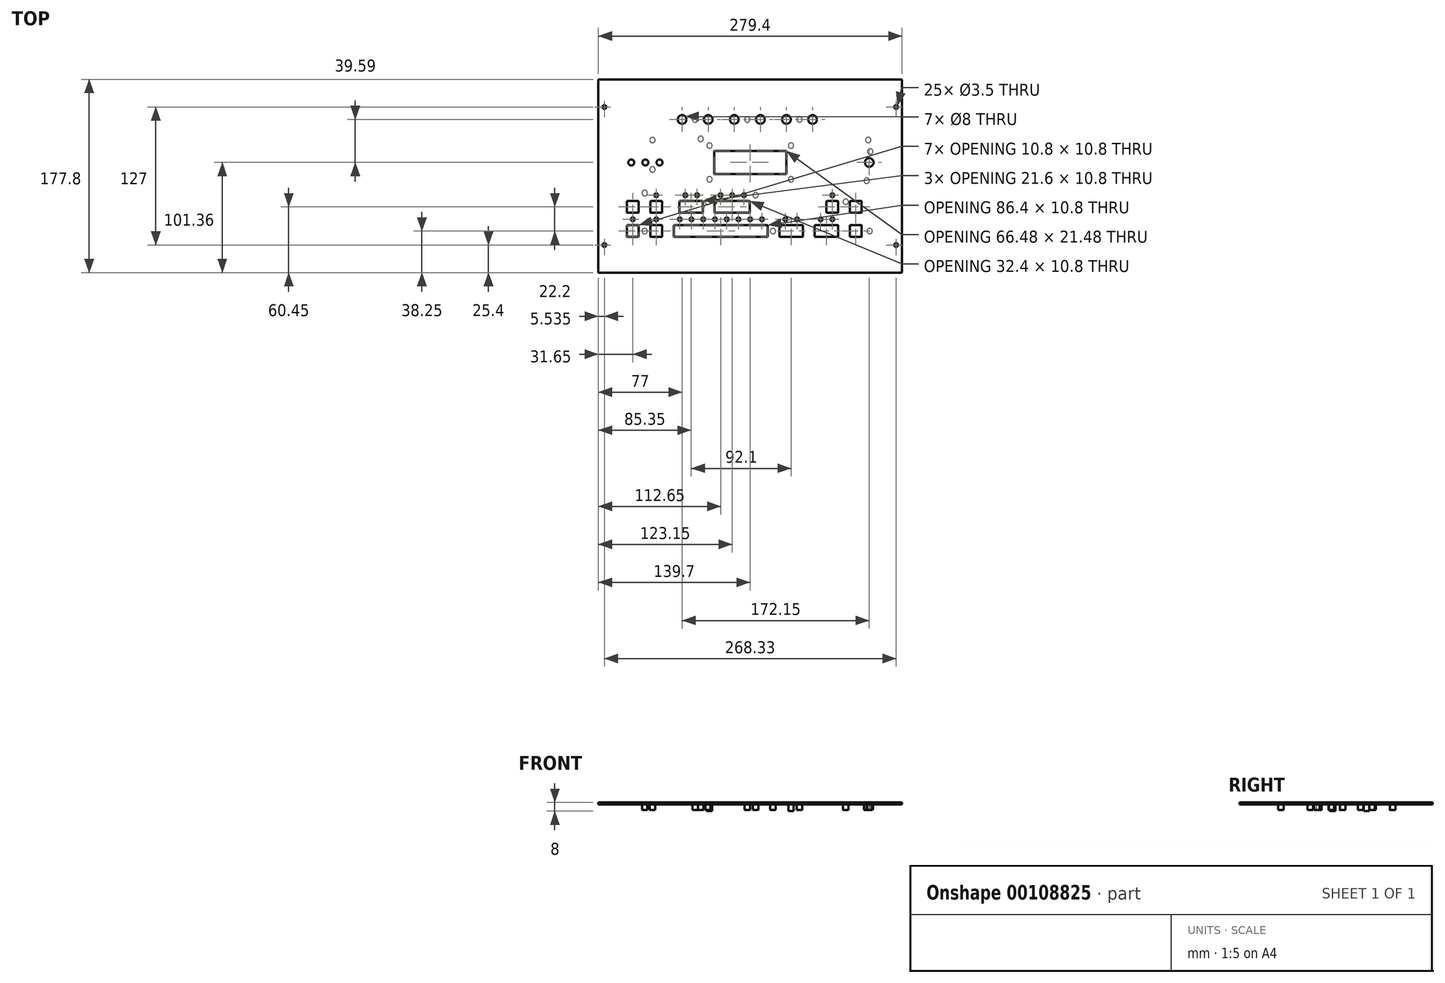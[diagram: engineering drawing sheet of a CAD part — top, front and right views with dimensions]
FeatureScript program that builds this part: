
annotation { "Feature Type Name" : "Feature", "Feature Type Description" : "" }
export const myFeature = defineFeature(function(context is Context, id is Id, definition is map)
    precondition{}
    {
        {
            var Q0;
            Q0=qCreatedBy(makeId("Top.planeOp"),FACE);
            var sketch = newSketch(context, id + "F0", { "sketchPlane" : qUnion([Q0])});
            skLineSegment(sketch, "E0", {"start": v(140.2, 89.4) * mm, "end": v(-139.2, 89.4) * mm});
            skLineSegment(sketch, "E1", {"start": v(-139.2, 89.4) * mm, "end": v(-139.2, -88.4) * mm});
            skLineSegment(sketch, "E2", {"start": v(-139.2, -88.4) * mm, "end": v(140.2, -88.4) * mm});
            skLineSegment(sketch, "E3", {"start": v(140.2, -88.4) * mm, "end": v(140.2, 89.4) * mm});
            skCircle(sketch, "E4", {"center": v(-133.66, 64) * mm, "radius": 1.75 * mm});
            skCircle(sketch, "E5", {"center": v(-133.66, -63) * mm, "radius": 1.75 * mm});
            skCircle(sketch, "E6", {"center": v(134.67, 64) * mm, "radius": 1.75 * mm});
            skCircle(sketch, "E7", {"center": v(134.67, -63) * mm, "radius": 1.75 * mm});
            skCircle(sketch, "E8", {"center": v(-108.95, 12.96) * mm, "radius": 2.75 * mm});
            skCircle(sketch, "E9", {"center": v(-62.2, 52.55) * mm, "radius": 4 * mm});
            skCircle(sketch, "E10", {"center": v(-38.2, 52.55) * mm, "radius": 4 * mm});
            skCircle(sketch, "E11", {"center": v(-14.2, 52.55) * mm, "radius": 4 * mm});
            skCircle(sketch, "E12", {"center": v(9.8, 52.55) * mm, "radius": 4 * mm});
            skCircle(sketch, "E13", {"center": v(33.8, 52.55) * mm, "radius": 4 * mm});
            skCircle(sketch, "E14", {"center": v(57.8, 52.55) * mm, "radius": 4 * mm});
            skCircle(sketch, "E15", {"center": v(109.95, 12.96) * mm, "radius": 4 * mm});
            skLineSegment(sketch, "E16", {"start": v(16.65, -45.25) * mm, "end": v(16.65, -55.05) * mm});
            skArc(sketch, "E17", {"start": v(16.15, -55.55) * mm, "mid": v(16.5, -55.4) * mm, "end": v(16.65, -55.05) * mm});
            skLineSegment(sketch, "E18", {"start": v(16.15, -55.55) * mm, "end": v(-69.25, -55.55) * mm});
            skArc(sketch, "E19", {"start": v(-69.75, -55.05) * mm, "mid": v(-69.6, -55.4) * mm, "end": v(-69.25, -55.55) * mm});
            skLineSegment(sketch, "E20", {"start": v(-69.75, -55.05) * mm, "end": v(-69.75, -45.25) * mm});
            skArc(sketch, "E21", {"start": v(-69.25, -44.75) * mm, "mid": v(-69.6, -44.9) * mm, "end": v(-69.75, -45.25) * mm});
            skLineSegment(sketch, "E22", {"start": v(-69.25, -44.75) * mm, "end": v(16.15, -44.75) * mm});
            skArc(sketch, "E23", {"start": v(16.65, -45.25) * mm, "mid": v(16.5, -44.9) * mm, "end": v(16.15, -44.75) * mm});
            skLineSegment(sketch, "E24", {"start": v(49.05, -45.25) * mm, "end": v(49.05, -55.05) * mm});
            skArc(sketch, "E25", {"start": v(48.55, -55.55) * mm, "mid": v(48.9, -55.4) * mm, "end": v(49.05, -55.05) * mm});
            skLineSegment(sketch, "E26", {"start": v(48.55, -55.55) * mm, "end": v(27.95, -55.55) * mm});
            skArc(sketch, "E27", {"start": v(27.45, -55.05) * mm, "mid": v(27.6, -55.4) * mm, "end": v(27.95, -55.55) * mm});
            skLineSegment(sketch, "E28", {"start": v(27.45, -55.05) * mm, "end": v(27.45, -45.25) * mm});
            skArc(sketch, "E29", {"start": v(27.95, -44.75) * mm, "mid": v(27.6, -44.9) * mm, "end": v(27.45, -45.25) * mm});
            skLineSegment(sketch, "E30", {"start": v(27.95, -44.75) * mm, "end": v(48.55, -44.75) * mm});
            skArc(sketch, "E31", {"start": v(49.05, -45.25) * mm, "mid": v(48.9, -44.9) * mm, "end": v(48.55, -44.75) * mm});
            skLineSegment(sketch, "E32", {"start": v(-102.15, -23.05) * mm, "end": v(-102.15, -32.85) * mm});
            skArc(sketch, "E33", {"start": v(-102.65, -33.35) * mm, "mid": v(-102.3, -33.2) * mm, "end": v(-102.15, -32.85) * mm});
            skLineSegment(sketch, "E34", {"start": v(-102.65, -33.35) * mm, "end": v(-112.45, -33.35) * mm});
            skArc(sketch, "E35", {"start": v(-112.95, -32.85) * mm, "mid": v(-112.8, -33.2) * mm, "end": v(-112.45, -33.35) * mm});
            skLineSegment(sketch, "E36", {"start": v(-112.95, -32.85) * mm, "end": v(-112.95, -23.05) * mm});
            skArc(sketch, "E37", {"start": v(-112.45, -22.55) * mm, "mid": v(-112.8, -22.7) * mm, "end": v(-112.95, -23.05) * mm});
            skLineSegment(sketch, "E38", {"start": v(-112.45, -22.55) * mm, "end": v(-102.65, -22.55) * mm});
            skArc(sketch, "E39", {"start": v(-102.15, -23.05) * mm, "mid": v(-102.3, -22.7) * mm, "end": v(-102.65, -22.55) * mm});
            skLineSegment(sketch, "E40", {"start": v(-80.55, -23.05) * mm, "end": v(-80.55, -32.85) * mm});
            skArc(sketch, "E41", {"start": v(-81.05, -33.35) * mm, "mid": v(-80.7, -33.2) * mm, "end": v(-80.55, -32.85) * mm});
            skLineSegment(sketch, "E42", {"start": v(-81.05, -33.35) * mm, "end": v(-90.85, -33.35) * mm});
            skArc(sketch, "E43", {"start": v(-91.35, -32.85) * mm, "mid": v(-91.2, -33.2) * mm, "end": v(-90.85, -33.35) * mm});
            skLineSegment(sketch, "E44", {"start": v(-91.35, -32.85) * mm, "end": v(-91.35, -23.05) * mm});
            skArc(sketch, "E45", {"start": v(-90.85, -22.55) * mm, "mid": v(-91.2, -22.7) * mm, "end": v(-91.35, -23.05) * mm});
            skLineSegment(sketch, "E46", {"start": v(-90.85, -22.55) * mm, "end": v(-81.05, -22.55) * mm});
            skArc(sketch, "E47", {"start": v(-80.55, -23.05) * mm, "mid": v(-80.7, -22.7) * mm, "end": v(-81.05, -22.55) * mm});
            skLineSegment(sketch, "E48", {"start": v(81.45, -23.05) * mm, "end": v(81.45, -32.85) * mm});
            skArc(sketch, "E49", {"start": v(80.95, -33.35) * mm, "mid": v(81.3, -33.2) * mm, "end": v(81.45, -32.85) * mm});
            skLineSegment(sketch, "E50", {"start": v(80.95, -33.35) * mm, "end": v(71.15, -33.35) * mm});
            skArc(sketch, "E51", {"start": v(70.65, -32.85) * mm, "mid": v(70.8, -33.2) * mm, "end": v(71.15, -33.35) * mm});
            skLineSegment(sketch, "E52", {"start": v(70.65, -32.85) * mm, "end": v(70.65, -23.05) * mm});
            skArc(sketch, "E53", {"start": v(71.15, -22.55) * mm, "mid": v(70.8, -22.7) * mm, "end": v(70.65, -23.05) * mm});
            skLineSegment(sketch, "E54", {"start": v(71.15, -22.55) * mm, "end": v(80.95, -22.55) * mm});
            skArc(sketch, "E55", {"start": v(81.45, -23.05) * mm, "mid": v(81.3, -22.7) * mm, "end": v(80.95, -22.55) * mm});
            skLineSegment(sketch, "E56", {"start": v(103.05, -23.05) * mm, "end": v(103.05, -32.85) * mm});
            skArc(sketch, "E57", {"start": v(102.55, -33.35) * mm, "mid": v(102.9, -33.2) * mm, "end": v(103.05, -32.85) * mm});
            skLineSegment(sketch, "E58", {"start": v(102.55, -33.35) * mm, "end": v(92.75, -33.35) * mm});
            skArc(sketch, "E59", {"start": v(92.25, -32.85) * mm, "mid": v(92.4, -33.2) * mm, "end": v(92.75, -33.35) * mm});
            skLineSegment(sketch, "E60", {"start": v(92.25, -32.85) * mm, "end": v(92.25, -23.05) * mm});
            skArc(sketch, "E61", {"start": v(92.75, -22.55) * mm, "mid": v(92.4, -22.7) * mm, "end": v(92.25, -23.05) * mm});
            skLineSegment(sketch, "E62", {"start": v(92.75, -22.55) * mm, "end": v(102.55, -22.55) * mm});
            skArc(sketch, "E63", {"start": v(103.05, -23.05) * mm, "mid": v(102.9, -22.7) * mm, "end": v(102.55, -22.55) * mm});
            skLineSegment(sketch, "E64", {"start": v(-102.15, -45.25) * mm, "end": v(-102.15, -55.05) * mm});
            skArc(sketch, "E65", {"start": v(-102.65, -55.55) * mm, "mid": v(-102.3, -55.4) * mm, "end": v(-102.15, -55.05) * mm});
            skLineSegment(sketch, "E66", {"start": v(-102.65, -55.55) * mm, "end": v(-112.45, -55.55) * mm});
            skArc(sketch, "E67", {"start": v(-112.95, -55.05) * mm, "mid": v(-112.8, -55.4) * mm, "end": v(-112.45, -55.55) * mm});
            skLineSegment(sketch, "E68", {"start": v(-112.95, -55.05) * mm, "end": v(-112.95, -45.25) * mm});
            skArc(sketch, "E69", {"start": v(-112.45, -44.75) * mm, "mid": v(-112.8, -44.9) * mm, "end": v(-112.95, -45.25) * mm});
            skLineSegment(sketch, "E70", {"start": v(-112.45, -44.75) * mm, "end": v(-102.65, -44.75) * mm});
            skArc(sketch, "E71", {"start": v(-102.15, -45.25) * mm, "mid": v(-102.3, -44.9) * mm, "end": v(-102.65, -44.75) * mm});
            skLineSegment(sketch, "E72", {"start": v(-80.55, -45.25) * mm, "end": v(-80.55, -55.05) * mm});
            skArc(sketch, "E73", {"start": v(-81.05, -55.55) * mm, "mid": v(-80.7, -55.4) * mm, "end": v(-80.55, -55.05) * mm});
            skLineSegment(sketch, "E74", {"start": v(-81.05, -55.55) * mm, "end": v(-90.85, -55.55) * mm});
            skArc(sketch, "E75", {"start": v(-91.35, -55.05) * mm, "mid": v(-91.2, -55.4) * mm, "end": v(-90.85, -55.55) * mm});
            skLineSegment(sketch, "E76", {"start": v(-91.35, -55.05) * mm, "end": v(-91.35, -45.25) * mm});
            skArc(sketch, "E77", {"start": v(-90.85, -44.75) * mm, "mid": v(-91.2, -44.9) * mm, "end": v(-91.35, -45.25) * mm});
            skLineSegment(sketch, "E78", {"start": v(-90.85, -44.75) * mm, "end": v(-81.05, -44.75) * mm});
            skArc(sketch, "E79", {"start": v(-80.55, -45.25) * mm, "mid": v(-80.7, -44.9) * mm, "end": v(-81.05, -44.75) * mm});
            skLineSegment(sketch, "E80", {"start": v(103.05, -45.25) * mm, "end": v(103.05, -55.05) * mm});
            skArc(sketch, "E81", {"start": v(102.55, -55.55) * mm, "mid": v(102.9, -55.4) * mm, "end": v(103.05, -55.05) * mm});
            skLineSegment(sketch, "E82", {"start": v(102.55, -55.55) * mm, "end": v(92.75, -55.55) * mm});
            skArc(sketch, "E83", {"start": v(92.25, -55.05) * mm, "mid": v(92.4, -55.4) * mm, "end": v(92.75, -55.55) * mm});
            skLineSegment(sketch, "E84", {"start": v(92.25, -55.05) * mm, "end": v(92.25, -45.25) * mm});
            skArc(sketch, "E85", {"start": v(92.75, -44.75) * mm, "mid": v(92.4, -44.9) * mm, "end": v(92.25, -45.25) * mm});
            skLineSegment(sketch, "E86", {"start": v(92.75, -44.75) * mm, "end": v(102.55, -44.75) * mm});
            skArc(sketch, "E87", {"start": v(103.05, -45.25) * mm, "mid": v(102.9, -44.9) * mm, "end": v(102.55, -44.75) * mm});
            skCircle(sketch, "E88", {"center": v(-85.95, -17.15) * mm, "radius": 1.75 * mm});
            skCircle(sketch, "E89", {"center": v(-59.25, -17.15) * mm, "radius": 1.75 * mm});
            skCircle(sketch, "E90", {"center": v(-48.45, -17.15) * mm, "radius": 1.75 * mm});
            skCircle(sketch, "E91", {"center": v(-26.85, -17.15) * mm, "radius": 1.75 * mm});
            skCircle(sketch, "E92", {"center": v(-16.05, -17.15) * mm, "radius": 1.75 * mm});
            skCircle(sketch, "E93", {"center": v(-5.25, -17.15) * mm, "radius": 1.75 * mm});
            skCircle(sketch, "E94", {"center": v(76.05, -17.15) * mm, "radius": 1.75 * mm});
            skCircle(sketch, "E95", {"center": v(-107.55, -39.35) * mm, "radius": 1.75 * mm});
            skCircle(sketch, "E96", {"center": v(-85.95, -39.35) * mm, "radius": 1.75 * mm});
            skCircle(sketch, "E97", {"center": v(-64.35, -39.35) * mm, "radius": 1.75 * mm});
            skCircle(sketch, "E98", {"center": v(-53.55, -39.35) * mm, "radius": 1.75 * mm});
            skCircle(sketch, "E99", {"center": v(-42.75, -39.35) * mm, "radius": 1.75 * mm});
            skCircle(sketch, "E100", {"center": v(-31.95, -39.35) * mm, "radius": 1.75 * mm});
            skCircle(sketch, "E101", {"center": v(-21.15, -39.35) * mm, "radius": 1.75 * mm});
            skCircle(sketch, "E102", {"center": v(-10.35, -39.35) * mm, "radius": 1.75 * mm});
            skCircle(sketch, "E103", {"center": v(0.45, -39.35) * mm, "radius": 1.75 * mm});
            skCircle(sketch, "E104", {"center": v(11.25, -39.35) * mm, "radius": 1.75 * mm});
            skCircle(sketch, "E105", {"center": v(32.85, -39.35) * mm, "radius": 1.75 * mm});
            skCircle(sketch, "E106", {"center": v(43.65, -39.35) * mm, "radius": 1.75 * mm});
            skCircle(sketch, "E107", {"center": v(65.25, -39.35) * mm, "radius": 1.75 * mm});
            skCircle(sketch, "E108", {"center": v(76.05, -39.35) * mm, "radius": 1.75 * mm});
            skLineSegment(sketch, "E109", {"start": v(-43.05, -23.05) * mm, "end": v(-43.05, -32.85) * mm});
            skArc(sketch, "E110", {"start": v(-43.55, -33.35) * mm, "mid": v(-43.2, -33.2) * mm, "end": v(-43.05, -32.85) * mm});
            skLineSegment(sketch, "E111", {"start": v(-43.55, -33.35) * mm, "end": v(-64.15, -33.35) * mm});
            skArc(sketch, "E112", {"start": v(-64.65, -32.85) * mm, "mid": v(-64.5, -33.2) * mm, "end": v(-64.15, -33.35) * mm});
            skLineSegment(sketch, "E113", {"start": v(-64.65, -32.85) * mm, "end": v(-64.65, -23.05) * mm});
            skArc(sketch, "E114", {"start": v(-64.15, -22.55) * mm, "mid": v(-64.5, -22.7) * mm, "end": v(-64.65, -23.05) * mm});
            skLineSegment(sketch, "E115", {"start": v(-64.15, -22.55) * mm, "end": v(-43.55, -22.55) * mm});
            skArc(sketch, "E116", {"start": v(-43.05, -23.05) * mm, "mid": v(-43.2, -22.7) * mm, "end": v(-43.55, -22.55) * mm});
            skLineSegment(sketch, "E117", {"start": v(81.45, -45.25) * mm, "end": v(81.45, -55.05) * mm});
            skArc(sketch, "E118", {"start": v(80.95, -55.55) * mm, "mid": v(81.3, -55.4) * mm, "end": v(81.45, -55.05) * mm});
            skLineSegment(sketch, "E119", {"start": v(80.95, -55.55) * mm, "end": v(60.35, -55.55) * mm});
            skArc(sketch, "E120", {"start": v(59.85, -55.05) * mm, "mid": v(60, -55.4) * mm, "end": v(60.35, -55.55) * mm});
            skLineSegment(sketch, "E121", {"start": v(59.85, -55.05) * mm, "end": v(59.85, -45.25) * mm});
            skArc(sketch, "E122", {"start": v(60.35, -44.75) * mm, "mid": v(60, -44.9) * mm, "end": v(59.85, -45.25) * mm});
            skLineSegment(sketch, "E123", {"start": v(60.35, -44.75) * mm, "end": v(80.95, -44.75) * mm});
            skArc(sketch, "E124", {"start": v(81.45, -45.25) * mm, "mid": v(81.3, -44.9) * mm, "end": v(80.95, -44.75) * mm});
            skLineSegment(sketch, "E125", {"start": v(0.15, -23.05) * mm, "end": v(0.15, -32.85) * mm});
            skArc(sketch, "E126", {"start": v(-0.35, -33.35) * mm, "mid": v(0, -33.2) * mm, "end": v(0.15, -32.85) * mm});
            skLineSegment(sketch, "E127", {"start": v(-0.35, -33.35) * mm, "end": v(-31.75, -33.35) * mm});
            skArc(sketch, "E128", {"start": v(-32.25, -32.85) * mm, "mid": v(-32.1, -33.2) * mm, "end": v(-31.75, -33.35) * mm});
            skLineSegment(sketch, "E129", {"start": v(-32.25, -32.85) * mm, "end": v(-32.25, -23.05) * mm});
            skArc(sketch, "E130", {"start": v(-31.75, -22.55) * mm, "mid": v(-32.1, -22.7) * mm, "end": v(-32.25, -23.05) * mm});
            skLineSegment(sketch, "E131", {"start": v(-31.75, -22.55) * mm, "end": v(-0.35, -22.55) * mm});
            skArc(sketch, "E132", {"start": v(0.15, -23.05) * mm, "mid": v(0, -22.7) * mm, "end": v(-0.35, -22.55) * mm});
            skCircle(sketch, "E133", {"center": v(-96.65, -50.15) * mm, "radius": 3.5 * mm});
            skCircle(sketch, "E134", {"center": v(-96.65, -50.15) * mm, "radius": 2.5 * mm});
            skCircle(sketch, "E135", {"center": v(-96.65, -50.15) * mm, "radius": 1.5 * mm});
            skCircle(sketch, "E136", {"center": v(-96.65, -15.15) * mm, "radius": 3.5 * mm});
            skCircle(sketch, "E137", {"center": v(-96.65, -15.15) * mm, "radius": 2.5 * mm});
            skCircle(sketch, "E138", {"center": v(-96.65, -15.15) * mm, "radius": 1.5 * mm});
            skCircle(sketch, "E139", {"center": v(-38.65, -23.15) * mm, "radius": 3.5 * mm});
            skCircle(sketch, "E140", {"center": v(-38.65, -23.15) * mm, "radius": 2.5 * mm});
            skCircle(sketch, "E141", {"center": v(-38.65, -23.15) * mm, "radius": 1.5 * mm});
            skCircle(sketch, "E142", {"center": v(21.35, -50.15) * mm, "radius": 3.5 * mm});
            skCircle(sketch, "E143", {"center": v(21.35, -50.15) * mm, "radius": 2.5 * mm});
            skCircle(sketch, "E144", {"center": v(21.35, -50.15) * mm, "radius": 1.5 * mm});
            skCircle(sketch, "E145", {"center": v(88.35, -23.15) * mm, "radius": 3.5 * mm});
            skCircle(sketch, "E146", {"center": v(88.35, -23.15) * mm, "radius": 2.5 * mm});
            skCircle(sketch, "E147", {"center": v(88.35, -23.15) * mm, "radius": 1.5 * mm});
            skCircle(sketch, "E148", {"center": v(110.35, -50.15) * mm, "radius": 3.5 * mm});
            skCircle(sketch, "E149", {"center": v(110.35, -50.15) * mm, "radius": 2.5 * mm});
            skCircle(sketch, "E150", {"center": v(110.35, -50.15) * mm, "radius": 1.5 * mm});
            skCircle(sketch, "E151", {"center": v(5.35, -17.15) * mm, "radius": 3.5 * mm});
            skCircle(sketch, "E152", {"center": v(5.35, -17.15) * mm, "radius": 2.5 * mm});
            skCircle(sketch, "E153", {"center": v(5.35, -17.15) * mm, "radius": 1.5 * mm});
            skCircle(sketch, "E154", {"center": v(-95.95, 12.96) * mm, "radius": 2.75 * mm});
            skCircle(sketch, "E155", {"center": v(-82.95, 12.96) * mm, "radius": 2.75 * mm});
            skCircle(sketch, "E156", {"center": v(109.05, 33.65) * mm, "radius": 3.5 * mm});
            skCircle(sketch, "E157", {"center": v(109.05, 33.65) * mm, "radius": 2.5 * mm});
            skCircle(sketch, "E158", {"center": v(109.05, 33.65) * mm, "radius": 1.5 * mm});
            skCircle(sketch, "E159", {"center": v(110.85, 23.05) * mm, "radius": 3.5 * mm});
            skCircle(sketch, "E160", {"center": v(110.85, 23.05) * mm, "radius": 2.5 * mm});
            skCircle(sketch, "E161", {"center": v(110.85, 23.05) * mm, "radius": 1.5 * mm});
            skCircle(sketch, "E162", {"center": v(107.6, -3.75) * mm, "radius": 3.5 * mm});
            skCircle(sketch, "E163", {"center": v(107.6, -3.75) * mm, "radius": 2.5 * mm});
            skCircle(sketch, "E164", {"center": v(107.6, -3.75) * mm, "radius": 1.5 * mm});
            skCircle(sketch, "E165", {"center": v(-89.45, 33.55) * mm, "radius": 3.5 * mm});
            skCircle(sketch, "E166", {"center": v(-89.45, 33.55) * mm, "radius": 2.5 * mm});
            skCircle(sketch, "E167", {"center": v(-89.45, 33.55) * mm, "radius": 1.5 * mm});
            skCircle(sketch, "E168", {"center": v(-89.45, 6.55) * mm, "radius": 3.5 * mm});
            skCircle(sketch, "E169", {"center": v(-89.45, 6.55) * mm, "radius": 2.5 * mm});
            skCircle(sketch, "E170", {"center": v(-89.45, 6.55) * mm, "radius": 1.5 * mm});
            skCircle(sketch, "E171", {"center": v(-45.05, 34.65) * mm, "radius": 3.5 * mm});
            skCircle(sketch, "E172", {"center": v(-45.05, 34.65) * mm, "radius": 2.5 * mm});
            skCircle(sketch, "E173", {"center": v(-45.05, 34.65) * mm, "radius": 1.5 * mm});
            skCircle(sketch, "E174", {"center": v(38, -2.54) * mm, "radius": 3.5 * mm});
            skCircle(sketch, "E175", {"center": v(38, -2.54) * mm, "radius": 2.5 * mm});
            skCircle(sketch, "E176", {"center": v(38, -2.54) * mm, "radius": 1.25 * mm});
            skArc(sketch, "E177", {"start": v(33.6, 22.85) * mm, "mid": v(33.6, 23.55) * mm, "end": v(32.9, 23.56) * mm});
            skLineSegment(sketch, "E178", {"start": v(33.6, 22.85) * mm, "end": v(33.6, 3.07) * mm});
            skArc(sketch, "E179", {"start": v(32.9, 2.36) * mm, "mid": v(33.6, 2.37) * mm, "end": v(33.6, 3.07) * mm});
            skLineSegment(sketch, "E180", {"start": v(32.9, 2.36) * mm, "end": v(-31.9, 2.36) * mm});
            skArc(sketch, "E181", {"start": v(-32.6, 3.07) * mm, "mid": v(-32.6, 2.37) * mm, "end": v(-31.9, 2.36) * mm});
            skLineSegment(sketch, "E182", {"start": v(-32.6, 3.07) * mm, "end": v(-32.6, 22.85) * mm});
            skArc(sketch, "E183", {"start": v(-31.9, 23.56) * mm, "mid": v(-32.6, 23.55) * mm, "end": v(-32.6, 22.85) * mm});
            skLineSegment(sketch, "E184", {"start": v(-31.9, 23.56) * mm, "end": v(32.9, 23.56) * mm});
            skCircle(sketch, "E185", {"center": v(-37, -2.54) * mm, "radius": 3.5 * mm});
            skCircle(sketch, "E186", {"center": v(-37, -2.54) * mm, "radius": 2.5 * mm});
            skCircle(sketch, "E187", {"center": v(-37, -2.54) * mm, "radius": 1.25 * mm});
            skCircle(sketch, "E188", {"center": v(-37, 28.46) * mm, "radius": 3.5 * mm});
            skCircle(sketch, "E189", {"center": v(-37, 28.46) * mm, "radius": 2.5 * mm});
            skCircle(sketch, "E190", {"center": v(-37, 28.46) * mm, "radius": 1.25 * mm});
            skCircle(sketch, "E191", {"center": v(38, 28.46) * mm, "radius": 3.5 * mm});
            skCircle(sketch, "E192", {"center": v(38, 28.46) * mm, "radius": 2.5 * mm});
            skCircle(sketch, "E193", {"center": v(38, 28.46) * mm, "radius": 1.25 * mm});
            skCircle(sketch, "E194", {"center": v(-50.2, 52.55) * mm, "radius": 3.5 * mm});
            skCircle(sketch, "E195", {"center": v(-50.2, 52.55) * mm, "radius": 2.5 * mm});
            skCircle(sketch, "E196", {"center": v(-50.2, 52.55) * mm, "radius": 1.5 * mm});
            skCircle(sketch, "E197", {"center": v(-2.2, 52.55) * mm, "radius": 3.5 * mm});
            skCircle(sketch, "E198", {"center": v(-2.2, 52.55) * mm, "radius": 2.5 * mm});
            skCircle(sketch, "E199", {"center": v(-2.2, 52.55) * mm, "radius": 1.5 * mm});
            skCircle(sketch, "E200", {"center": v(45.8, 52.55) * mm, "radius": 3.5 * mm});
            skCircle(sketch, "E201", {"center": v(45.8, 52.55) * mm, "radius": 2.5 * mm});
            skCircle(sketch, "E202", {"center": v(45.8, 52.55) * mm, "radius": 1.5 * mm});
            skLineSegment(sketch, "E203", {"start": v(-140.2, -88.4) * mm, "end": v(-138.2, -88.4) * mm});
            skLineSegment(sketch, "E204", {"start": v(-139.2, -89.4) * mm, "end": v(-139.2, -87.4) * mm});
            skLineSegment(sketch, "E205", {"start": v(-134.67, 64) * mm, "end": v(-132.66, 64) * mm});
            skLineSegment(sketch, "E206", {"start": v(-133.66, 63) * mm, "end": v(-133.66, 65) * mm});
            skLineSegment(sketch, "E207", {"start": v(-134.67, -63) * mm, "end": v(-132.66, -63) * mm});
            skLineSegment(sketch, "E208", {"start": v(-133.66, -64) * mm, "end": v(-133.66, -62) * mm});
            skLineSegment(sketch, "E209", {"start": v(133.67, 64) * mm, "end": v(135.67, 64) * mm});
            skLineSegment(sketch, "E210", {"start": v(134.67, 63) * mm, "end": v(134.67, 65) * mm});
            skLineSegment(sketch, "E211", {"start": v(133.67, -63) * mm, "end": v(135.67, -63) * mm});
            skLineSegment(sketch, "E212", {"start": v(134.67, -64) * mm, "end": v(134.67, -62) * mm});
            skLineSegment(sketch, "E213", {"start": v(-109.95, 12.96) * mm, "end": v(-107.95, 12.96) * mm});
            skLineSegment(sketch, "E214", {"start": v(-108.95, 11.96) * mm, "end": v(-108.95, 13.96) * mm});
            skLineSegment(sketch, "E215", {"start": v(-63.2, 52.55) * mm, "end": v(-61.2, 52.55) * mm});
            skLineSegment(sketch, "E216", {"start": v(-62.2, 51.55) * mm, "end": v(-62.2, 53.55) * mm});
            skLineSegment(sketch, "E217", {"start": v(-39.2, 52.55) * mm, "end": v(-37.2, 52.55) * mm});
            skLineSegment(sketch, "E218", {"start": v(-38.2, 51.55) * mm, "end": v(-38.2, 53.55) * mm});
            skLineSegment(sketch, "E219", {"start": v(-15.2, 52.55) * mm, "end": v(-13.2, 52.55) * mm});
            skLineSegment(sketch, "E220", {"start": v(-14.2, 51.55) * mm, "end": v(-14.2, 53.55) * mm});
            skLineSegment(sketch, "E221", {"start": v(8.8, 52.55) * mm, "end": v(10.8, 52.55) * mm});
            skLineSegment(sketch, "E222", {"start": v(9.8, 51.55) * mm, "end": v(9.8, 53.55) * mm});
            skLineSegment(sketch, "E223", {"start": v(32.8, 52.55) * mm, "end": v(34.8, 52.55) * mm});
            skLineSegment(sketch, "E224", {"start": v(33.8, 51.55) * mm, "end": v(33.8, 53.55) * mm});
            skLineSegment(sketch, "E225", {"start": v(56.8, 52.55) * mm, "end": v(58.8, 52.55) * mm});
            skLineSegment(sketch, "E226", {"start": v(57.8, 51.55) * mm, "end": v(57.8, 53.55) * mm});
            skLineSegment(sketch, "E227", {"start": v(108.95, 12.96) * mm, "end": v(110.95, 12.96) * mm});
            skLineSegment(sketch, "E228", {"start": v(109.95, 11.96) * mm, "end": v(109.95, 13.96) * mm});
            skLineSegment(sketch, "E229", {"start": v(-27.55, -50.15) * mm, "end": v(-25.55, -50.15) * mm});
            skLineSegment(sketch, "E230", {"start": v(-26.55, -51.15) * mm, "end": v(-26.55, -49.15) * mm});
            skLineSegment(sketch, "E231", {"start": v(37.25, -50.15) * mm, "end": v(39.25, -50.15) * mm});
            skLineSegment(sketch, "E232", {"start": v(38.25, -51.15) * mm, "end": v(38.25, -49.15) * mm});
            skLineSegment(sketch, "E233", {"start": v(-108.55, -27.95) * mm, "end": v(-106.55, -27.95) * mm});
            skLineSegment(sketch, "E234", {"start": v(-107.55, -28.95) * mm, "end": v(-107.55, -26.95) * mm});
            skLineSegment(sketch, "E235", {"start": v(-86.95, -27.95) * mm, "end": v(-84.95, -27.95) * mm});
            skLineSegment(sketch, "E236", {"start": v(-85.95, -28.95) * mm, "end": v(-85.95, -26.95) * mm});
            skLineSegment(sketch, "E237", {"start": v(75.05, -27.95) * mm, "end": v(77.05, -27.95) * mm});
            skLineSegment(sketch, "E238", {"start": v(76.05, -28.95) * mm, "end": v(76.05, -26.95) * mm});
            skLineSegment(sketch, "E239", {"start": v(96.65, -27.95) * mm, "end": v(98.65, -27.95) * mm});
            skLineSegment(sketch, "E240", {"start": v(97.65, -28.95) * mm, "end": v(97.65, -26.95) * mm});
            skLineSegment(sketch, "E241", {"start": v(-108.55, -50.15) * mm, "end": v(-106.55, -50.15) * mm});
            skLineSegment(sketch, "E242", {"start": v(-107.55, -51.15) * mm, "end": v(-107.55, -49.15) * mm});
            skLineSegment(sketch, "E243", {"start": v(-86.95, -50.15) * mm, "end": v(-84.95, -50.15) * mm});
            skLineSegment(sketch, "E244", {"start": v(-85.95, -51.15) * mm, "end": v(-85.95, -49.15) * mm});
            skLineSegment(sketch, "E245", {"start": v(96.65, -50.15) * mm, "end": v(98.65, -50.15) * mm});
            skLineSegment(sketch, "E246", {"start": v(97.65, -51.15) * mm, "end": v(97.65, -49.15) * mm});
            skLineSegment(sketch, "E247", {"start": v(-86.95, -17.15) * mm, "end": v(-84.95, -17.15) * mm});
            skLineSegment(sketch, "E248", {"start": v(-85.95, -18.15) * mm, "end": v(-85.95, -16.15) * mm});
            skLineSegment(sketch, "E249", {"start": v(-60.25, -17.15) * mm, "end": v(-58.25, -17.15) * mm});
            skLineSegment(sketch, "E250", {"start": v(-59.25, -18.15) * mm, "end": v(-59.25, -16.15) * mm});
            skLineSegment(sketch, "E251", {"start": v(-49.45, -17.15) * mm, "end": v(-47.45, -17.15) * mm});
            skLineSegment(sketch, "E252", {"start": v(-48.45, -18.15) * mm, "end": v(-48.45, -16.15) * mm});
            skLineSegment(sketch, "E253", {"start": v(-27.85, -17.15) * mm, "end": v(-25.85, -17.15) * mm});
            skLineSegment(sketch, "E254", {"start": v(-26.85, -18.15) * mm, "end": v(-26.85, -16.15) * mm});
            skLineSegment(sketch, "E255", {"start": v(-17.05, -17.15) * mm, "end": v(-15.05, -17.15) * mm});
            skLineSegment(sketch, "E256", {"start": v(-16.05, -18.15) * mm, "end": v(-16.05, -16.15) * mm});
            skLineSegment(sketch, "E257", {"start": v(-6.25, -17.15) * mm, "end": v(-4.25, -17.15) * mm});
            skLineSegment(sketch, "E258", {"start": v(-5.25, -18.15) * mm, "end": v(-5.25, -16.15) * mm});
            skLineSegment(sketch, "E259", {"start": v(75.05, -17.15) * mm, "end": v(77.05, -17.15) * mm});
            skLineSegment(sketch, "E260", {"start": v(76.05, -18.15) * mm, "end": v(76.05, -16.15) * mm});
            skLineSegment(sketch, "E261", {"start": v(-108.55, -39.35) * mm, "end": v(-106.55, -39.35) * mm});
            skLineSegment(sketch, "E262", {"start": v(-107.55, -40.35) * mm, "end": v(-107.55, -38.35) * mm});
            skLineSegment(sketch, "E263", {"start": v(-86.95, -39.35) * mm, "end": v(-84.95, -39.35) * mm});
            skLineSegment(sketch, "E264", {"start": v(-85.95, -40.35) * mm, "end": v(-85.95, -38.35) * mm});
            skLineSegment(sketch, "E265", {"start": v(-65.35, -39.35) * mm, "end": v(-63.35, -39.35) * mm});
            skLineSegment(sketch, "E266", {"start": v(-64.35, -40.35) * mm, "end": v(-64.35, -38.35) * mm});
            skLineSegment(sketch, "E267", {"start": v(-54.55, -39.35) * mm, "end": v(-52.55, -39.35) * mm});
            skLineSegment(sketch, "E268", {"start": v(-53.55, -40.35) * mm, "end": v(-53.55, -38.35) * mm});
            skLineSegment(sketch, "E269", {"start": v(-43.75, -39.35) * mm, "end": v(-41.75, -39.35) * mm});
            skLineSegment(sketch, "E270", {"start": v(-42.75, -40.35) * mm, "end": v(-42.75, -38.35) * mm});
            skLineSegment(sketch, "E271", {"start": v(-32.95, -39.35) * mm, "end": v(-30.95, -39.35) * mm});
            skLineSegment(sketch, "E272", {"start": v(-31.95, -40.35) * mm, "end": v(-31.95, -38.35) * mm});
            skLineSegment(sketch, "E273", {"start": v(-22.15, -39.35) * mm, "end": v(-20.15, -39.35) * mm});
            skLineSegment(sketch, "E274", {"start": v(-21.15, -40.35) * mm, "end": v(-21.15, -38.35) * mm});
            skLineSegment(sketch, "E275", {"start": v(-11.35, -39.35) * mm, "end": v(-9.35, -39.35) * mm});
            skLineSegment(sketch, "E276", {"start": v(-10.35, -40.35) * mm, "end": v(-10.35, -38.35) * mm});
            skLineSegment(sketch, "E277", {"start": v(-0.55, -39.35) * mm, "end": v(1.45, -39.35) * mm});
            skLineSegment(sketch, "E278", {"start": v(0.45, -40.35) * mm, "end": v(0.45, -38.35) * mm});
            skLineSegment(sketch, "E279", {"start": v(10.25, -39.35) * mm, "end": v(12.25, -39.35) * mm});
            skLineSegment(sketch, "E280", {"start": v(11.25, -40.35) * mm, "end": v(11.25, -38.35) * mm});
            skLineSegment(sketch, "E281", {"start": v(31.85, -39.35) * mm, "end": v(33.85, -39.35) * mm});
            skLineSegment(sketch, "E282", {"start": v(32.85, -40.35) * mm, "end": v(32.85, -38.35) * mm});
            skLineSegment(sketch, "E283", {"start": v(42.65, -39.35) * mm, "end": v(44.65, -39.35) * mm});
            skLineSegment(sketch, "E284", {"start": v(43.65, -40.35) * mm, "end": v(43.65, -38.35) * mm});
            skLineSegment(sketch, "E285", {"start": v(64.25, -39.35) * mm, "end": v(66.25, -39.35) * mm});
            skLineSegment(sketch, "E286", {"start": v(65.25, -40.35) * mm, "end": v(65.25, -38.35) * mm});
            skLineSegment(sketch, "E287", {"start": v(75.05, -39.35) * mm, "end": v(77.05, -39.35) * mm});
            skLineSegment(sketch, "E288", {"start": v(76.05, -40.35) * mm, "end": v(76.05, -38.35) * mm});
            skLineSegment(sketch, "E289", {"start": v(-54.85, -27.95) * mm, "end": v(-52.85, -27.95) * mm});
            skLineSegment(sketch, "E290", {"start": v(-53.85, -28.95) * mm, "end": v(-53.85, -26.95) * mm});
            skLineSegment(sketch, "E291", {"start": v(69.65, -50.15) * mm, "end": v(71.65, -50.15) * mm});
            skLineSegment(sketch, "E292", {"start": v(70.65, -51.15) * mm, "end": v(70.65, -49.15) * mm});
            skLineSegment(sketch, "E293", {"start": v(-17.05, -27.95) * mm, "end": v(-15.05, -27.95) * mm});
            skLineSegment(sketch, "E294", {"start": v(-16.05, -28.95) * mm, "end": v(-16.05, -26.95) * mm});
            skLineSegment(sketch, "E295", {"start": v(-97.65, -50.15) * mm, "end": v(-95.65, -50.15) * mm});
            skLineSegment(sketch, "E296", {"start": v(-96.65, -51.15) * mm, "end": v(-96.65, -49.15) * mm});
            skLineSegment(sketch, "E297", {"start": v(-97.65, -15.15) * mm, "end": v(-95.65, -15.15) * mm});
            skLineSegment(sketch, "E298", {"start": v(-96.65, -16.15) * mm, "end": v(-96.65, -14.15) * mm});
            skLineSegment(sketch, "E299", {"start": v(-39.65, -23.15) * mm, "end": v(-37.65, -23.15) * mm});
            skLineSegment(sketch, "E300", {"start": v(-38.65, -24.15) * mm, "end": v(-38.65, -22.15) * mm});
            skLineSegment(sketch, "E301", {"start": v(20.35, -50.15) * mm, "end": v(22.35, -50.15) * mm});
            skLineSegment(sketch, "E302", {"start": v(21.35, -51.15) * mm, "end": v(21.35, -49.15) * mm});
            skLineSegment(sketch, "E303", {"start": v(87.35, -23.15) * mm, "end": v(89.35, -23.15) * mm});
            skLineSegment(sketch, "E304", {"start": v(88.35, -24.15) * mm, "end": v(88.35, -22.15) * mm});
            skLineSegment(sketch, "E305", {"start": v(109.35, -50.15) * mm, "end": v(111.35, -50.15) * mm});
            skLineSegment(sketch, "E306", {"start": v(110.35, -51.15) * mm, "end": v(110.35, -49.15) * mm});
            skLineSegment(sketch, "E307", {"start": v(4.35, -17.15) * mm, "end": v(6.35, -17.15) * mm});
            skLineSegment(sketch, "E308", {"start": v(5.35, -18.15) * mm, "end": v(5.35, -16.15) * mm});
            skLineSegment(sketch, "E309", {"start": v(-96.95, 12.96) * mm, "end": v(-94.95, 12.96) * mm});
            skLineSegment(sketch, "E310", {"start": v(-95.95, 11.96) * mm, "end": v(-95.95, 13.96) * mm});
            skLineSegment(sketch, "E311", {"start": v(-83.95, 12.96) * mm, "end": v(-81.95, 12.96) * mm});
            skLineSegment(sketch, "E312", {"start": v(-82.95, 11.96) * mm, "end": v(-82.95, 13.96) * mm});
            skLineSegment(sketch, "E313", {"start": v(108.05, 33.65) * mm, "end": v(110.05, 33.65) * mm});
            skLineSegment(sketch, "E314", {"start": v(109.05, 32.65) * mm, "end": v(109.05, 34.65) * mm});
            skLineSegment(sketch, "E315", {"start": v(109.85, 23.05) * mm, "end": v(111.85, 23.05) * mm});
            skLineSegment(sketch, "E316", {"start": v(110.85, 22.05) * mm, "end": v(110.85, 24.05) * mm});
            skLineSegment(sketch, "E317", {"start": v(106.6, -3.75) * mm, "end": v(108.6, -3.75) * mm});
            skLineSegment(sketch, "E318", {"start": v(107.6, -4.75) * mm, "end": v(107.6, -2.75) * mm});
            skLineSegment(sketch, "E319", {"start": v(-90.45, 33.55) * mm, "end": v(-88.45, 33.55) * mm});
            skLineSegment(sketch, "E320", {"start": v(-89.45, 32.55) * mm, "end": v(-89.45, 34.55) * mm});
            skLineSegment(sketch, "E321", {"start": v(-90.45, 6.55) * mm, "end": v(-88.45, 6.55) * mm});
            skLineSegment(sketch, "E322", {"start": v(-89.45, 5.55) * mm, "end": v(-89.45, 7.55) * mm});
            skLineSegment(sketch, "E323", {"start": v(-46.05, 34.65) * mm, "end": v(-44.05, 34.65) * mm});
            skLineSegment(sketch, "E324", {"start": v(-45.05, 33.65) * mm, "end": v(-45.05, 35.65) * mm});
            skLineSegment(sketch, "E325", {"start": v(37, -2.54) * mm, "end": v(39, -2.54) * mm});
            skLineSegment(sketch, "E326", {"start": v(38, -3.54) * mm, "end": v(38, -1.54) * mm});
            skLineSegment(sketch, "E327", {"start": v(-0.5, 12.96) * mm, "end": v(1.5, 12.96) * mm});
            skLineSegment(sketch, "E328", {"start": v(0.5, 11.96) * mm, "end": v(0.5, 13.96) * mm});
            skLineSegment(sketch, "E329", {"start": v(-38, -2.54) * mm, "end": v(-36, -2.54) * mm});
            skLineSegment(sketch, "E330", {"start": v(-37, -3.54) * mm, "end": v(-37, -1.54) * mm});
            skLineSegment(sketch, "E331", {"start": v(-38, 28.46) * mm, "end": v(-36, 28.46) * mm});
            skLineSegment(sketch, "E332", {"start": v(-37, 27.46) * mm, "end": v(-37, 29.46) * mm});
            skLineSegment(sketch, "E333", {"start": v(37, 28.46) * mm, "end": v(39, 28.46) * mm});
            skLineSegment(sketch, "E334", {"start": v(38, 27.46) * mm, "end": v(38, 29.46) * mm});
            skLineSegment(sketch, "E335", {"start": v(-51.2, 52.55) * mm, "end": v(-49.2, 52.55) * mm});
            skLineSegment(sketch, "E336", {"start": v(-50.2, 51.55) * mm, "end": v(-50.2, 53.55) * mm});
            skLineSegment(sketch, "E337", {"start": v(-3.2, 52.55) * mm, "end": v(-1.2, 52.55) * mm});
            skLineSegment(sketch, "E338", {"start": v(-2.2, 51.55) * mm, "end": v(-2.2, 53.55) * mm});
            skLineSegment(sketch, "E339", {"start": v(44.8, 52.55) * mm, "end": v(46.8, 52.55) * mm});
            skLineSegment(sketch, "E340", {"start": v(45.8, 51.55) * mm, "end": v(45.8, 53.55) * mm});
            skLineSegment(sketch, "E341", {"start": v(-0.5, 0.5) * mm, "end": v(1.5, 0.5) * mm});
            skLineSegment(sketch, "E342", {"start": v(0.5, -0.5) * mm, "end": v(0.5, 1.5) * mm});
            skSolve(sketch);
        }
        {
            var Q0;
            {var subQ5=sQuery(id+"F0.wireOp",EDGE,"E0");Q0=makeQuery(id+"F0.imprint","IMPRINT",FACE,{"disambiguationData":[TD([[makeQuery(id+"F0.imprint","IMPRINT",EDGE,{"derivedFrom":subQ5}),1.0]])]});}
            var sketch = newSketch(context, id + "F1", { "sketchPlane" : qUnion([Q0])});
            skCircle(sketch, "E343.0", {"center": v(-62.2, 52.55) * mm, "radius": 4 * mm});
            skCircle(sketch, "E344.0", {"center": v(-38.2, 52.55) * mm, "radius": 4 * mm});
            skLineSegment(sketch, "E345.0", {"start": v(140.2, 89.4) * mm, "end": v(-139.2, 89.4) * mm});
            skLineSegment(sketch, "E346.0", {"start": v(-139.2, 89.4) * mm, "end": v(-139.2, -88.4) * mm});
            skLineSegment(sketch, "E347.0", {"start": v(140.2, -88.4) * mm, "end": v(140.2, 89.4) * mm});
            skLineSegment(sketch, "E348.0", {"start": v(-139.2, -88.4) * mm, "end": v(140.2, -88.4) * mm});
            skCircle(sketch, "E349.0", {"center": v(-14.2, 52.55) * mm, "radius": 4 * mm});
            skCircle(sketch, "E350.0", {"center": v(9.8, 52.55) * mm, "radius": 4 * mm});
            skCircle(sketch, "E351.0", {"center": v(33.8, 52.55) * mm, "radius": 4 * mm});
            skCircle(sketch, "E352.0", {"center": v(57.8, 52.55) * mm, "radius": 4 * mm});
            skPoint(sketch, "E353.0", {"position": v(135.67, 64) * mm});
            skCircle(sketch, "E354.0", {"center": v(134.67, -63) * mm, "radius": 1.75 * mm});
            skCircle(sketch, "E355.0", {"center": v(-133.66, -63) * mm, "radius": 1.75 * mm});
            skCircle(sketch, "E356.0", {"center": v(-133.66, 64) * mm, "radius": 1.75 * mm});
            skCircle(sketch, "E357.0", {"center": v(-108.95, 12.96) * mm, "radius": 2.75 * mm});
            skCircle(sketch, "E358.0", {"center": v(-95.95, 12.96) * mm, "radius": 2.75 * mm});
            skCircle(sketch, "E359.0", {"center": v(-82.95, 12.96) * mm, "radius": 2.75 * mm});
            skCircle(sketch, "E360.0", {"center": v(-107.55, -39.35) * mm, "radius": 1.75 * mm});
            skCircle(sketch, "E361.0", {"center": v(-85.95, -39.35) * mm, "radius": 1.75 * mm});
            skCircle(sketch, "E362.0", {"center": v(-85.95, -17.15) * mm, "radius": 1.75 * mm});
            skPoint(sketch, "E363.0", {"position": v(-59.25, -18.15) * mm});
            skCircle(sketch, "E364.0", {"center": v(-59.25, -17.15) * mm, "radius": 1.75 * mm});
            skCircle(sketch, "E365.0", {"center": v(-48.45, -17.15) * mm, "radius": 1.75 * mm});
            skCircle(sketch, "E366.0", {"center": v(-26.85, -17.15) * mm, "radius": 1.75 * mm});
            skCircle(sketch, "E367.0", {"center": v(-16.05, -17.15) * mm, "radius": 1.75 * mm});
            skCircle(sketch, "E368.0", {"center": v(-5.25, -17.15) * mm, "radius": 1.75 * mm});
            skLineSegment(sketch, "E369.0.1", {"start": v(-139.2, -88.4) * mm, "end": v(-138.2, -88.4) * mm});
            skLineSegment(sketch, "E369.0.2", {"start": v(-138.2, -88.4) * mm, "end": v(140.2, -88.4) * mm});
            skCircle(sketch, "E370.0", {"center": v(-53.55, -39.35) * mm, "radius": 1.75 * mm});
            skCircle(sketch, "E371.0", {"center": v(-64.35, -39.35) * mm, "radius": 1.75 * mm});
            skCircle(sketch, "E372.0", {"center": v(-42.75, -39.35) * mm, "radius": 1.75 * mm});
            skCircle(sketch, "E373.0", {"center": v(-31.95, -39.35) * mm, "radius": 1.75 * mm});
            skCircle(sketch, "E374.0", {"center": v(-21.15, -39.35) * mm, "radius": 1.75 * mm});
            skCircle(sketch, "E375.0", {"center": v(-10.35, -39.35) * mm, "radius": 1.75 * mm});
            skCircle(sketch, "E376.0", {"center": v(0.45, -39.35) * mm, "radius": 1.75 * mm});
            skCircle(sketch, "E377.0", {"center": v(11.25, -39.35) * mm, "radius": 1.75 * mm});
            skCircle(sketch, "E378.0", {"center": v(32.85, -39.35) * mm, "radius": 1.75 * mm});
            skCircle(sketch, "E379.0", {"center": v(76.05, -39.35) * mm, "radius": 1.75 * mm});
            skCircle(sketch, "E380.0", {"center": v(65.25, -39.35) * mm, "radius": 1.75 * mm});
            skCircle(sketch, "E381.0", {"center": v(76.05, -17.15) * mm, "radius": 1.75 * mm});
            skCircle(sketch, "E382.0", {"center": v(43.65, -39.35) * mm, "radius": 1.75 * mm});
            skCircle(sketch, "E383.0", {"center": v(109.95, 12.96) * mm, "radius": 4 * mm});
            skLineSegment(sketch, "E384.0", {"start": v(-31.9, 23.56) * mm, "end": v(32.9, 23.56) * mm});
            skLineSegment(sketch, "E384.1", {"start": v(32.9, 2.36) * mm, "end": v(-31.9, 2.36) * mm});
            skLineSegment(sketch, "E384.2", {"start": v(33.6, 22.85) * mm, "end": v(33.6, 3.07) * mm});
            skLineSegment(sketch, "E384.3", {"start": v(-32.6, 3.07) * mm, "end": v(-32.6, 22.85) * mm});
            skLineSegment(sketch, "E384.4", {"start": v(0.5, 11.96) * mm, "end": v(0.5, 13.96) * mm});
            skLineSegment(sketch, "E384.5", {"start": v(-0.5, 12.96) * mm, "end": v(1.5, 12.96) * mm});
            skArc(sketch, "E384.6", {"start": v(32.9, 2.36) * mm, "mid": v(33.6, 2.37) * mm, "end": v(33.6, 3.07) * mm});
            skArc(sketch, "E384.7", {"start": v(33.6, 22.85) * mm, "mid": v(33.6, 23.55) * mm, "end": v(32.9, 23.56) * mm});
            skArc(sketch, "E384.8", {"start": v(-32.6, 3.07) * mm, "mid": v(-32.6, 2.37) * mm, "end": v(-31.9, 2.36) * mm});
            skArc(sketch, "E384.9", {"start": v(-31.9, 23.56) * mm, "mid": v(-32.6, 23.55) * mm, "end": v(-32.6, 22.85) * mm});
            skLineSegment(sketch, "E385.0", {"start": v(27.45, -55.05) * mm, "end": v(27.45, -45.25) * mm});
            skLineSegment(sketch, "E385.1", {"start": v(60.35, -44.75) * mm, "end": v(80.95, -44.75) * mm});
            skLineSegment(sketch, "E385.2", {"start": v(103.05, -45.25) * mm, "end": v(103.05, -55.05) * mm});
            skLineSegment(sketch, "E385.3", {"start": v(49.05, -45.25) * mm, "end": v(49.05, -55.05) * mm});
            skLineSegment(sketch, "E385.4", {"start": v(80.95, -55.55) * mm, "end": v(60.35, -55.55) * mm});
            skLineSegment(sketch, "E385.5", {"start": v(92.75, -44.75) * mm, "end": v(102.55, -44.75) * mm});
            skLineSegment(sketch, "E385.6", {"start": v(81.45, -45.25) * mm, "end": v(81.45, -55.05) * mm});
            skLineSegment(sketch, "E385.7", {"start": v(48.55, -55.55) * mm, "end": v(27.95, -55.55) * mm});
            skLineSegment(sketch, "E385.8", {"start": v(59.85, -55.05) * mm, "end": v(59.85, -45.25) * mm});
            skLineSegment(sketch, "E385.9", {"start": v(102.55, -55.55) * mm, "end": v(92.75, -55.55) * mm});
            skLineSegment(sketch, "E385.10", {"start": v(92.25, -55.05) * mm, "end": v(92.25, -45.25) * mm});
            skLineSegment(sketch, "E385.11", {"start": v(27.95, -44.75) * mm, "end": v(48.55, -44.75) * mm});
            skLineSegment(sketch, "E385.12", {"start": v(38.25, -51.15) * mm, "end": v(38.25, -49.15) * mm});
            skLineSegment(sketch, "E385.13", {"start": v(69.65, -50.15) * mm, "end": v(71.65, -50.15) * mm});
            skLineSegment(sketch, "E385.14", {"start": v(37.25, -50.15) * mm, "end": v(39.25, -50.15) * mm});
            skLineSegment(sketch, "E385.15", {"start": v(70.65, -51.15) * mm, "end": v(70.65, -49.15) * mm});
            skLineSegment(sketch, "E385.16", {"start": v(96.65, -50.15) * mm, "end": v(98.65, -50.15) * mm});
            skLineSegment(sketch, "E385.17", {"start": v(97.65, -51.15) * mm, "end": v(97.65, -49.15) * mm});
            skArc(sketch, "E385.18", {"start": v(27.45, -55.05) * mm, "mid": v(27.6, -55.4) * mm, "end": v(27.95, -55.55) * mm});
            skArc(sketch, "E385.19", {"start": v(48.55, -55.55) * mm, "mid": v(48.9, -55.4) * mm, "end": v(49.05, -55.05) * mm});
            skArc(sketch, "E385.20", {"start": v(92.75, -44.75) * mm, "mid": v(92.4, -44.9) * mm, "end": v(92.25, -45.25) * mm});
            skArc(sketch, "E385.21", {"start": v(49.05, -45.25) * mm, "mid": v(48.9, -44.9) * mm, "end": v(48.55, -44.75) * mm});
            skArc(sketch, "E385.22", {"start": v(60.35, -44.75) * mm, "mid": v(60, -44.9) * mm, "end": v(59.85, -45.25) * mm});
            skArc(sketch, "E385.23", {"start": v(81.45, -45.25) * mm, "mid": v(81.3, -44.9) * mm, "end": v(80.95, -44.75) * mm});
            skArc(sketch, "E385.24", {"start": v(80.95, -55.55) * mm, "mid": v(81.3, -55.4) * mm, "end": v(81.45, -55.05) * mm});
            skArc(sketch, "E385.25", {"start": v(102.55, -55.55) * mm, "mid": v(102.9, -55.4) * mm, "end": v(103.05, -55.05) * mm});
            skArc(sketch, "E385.26", {"start": v(27.95, -44.75) * mm, "mid": v(27.6, -44.9) * mm, "end": v(27.45, -45.25) * mm});
            skArc(sketch, "E385.27", {"start": v(59.85, -55.05) * mm, "mid": v(60, -55.4) * mm, "end": v(60.35, -55.55) * mm});
            skArc(sketch, "E385.28", {"start": v(103.05, -45.25) * mm, "mid": v(102.9, -44.9) * mm, "end": v(102.55, -44.75) * mm});
            skArc(sketch, "E385.29", {"start": v(92.25, -55.05) * mm, "mid": v(92.4, -55.4) * mm, "end": v(92.75, -55.55) * mm});
            skArc(sketch, "E386.0", {"start": v(102.55, -33.35) * mm, "mid": v(102.9, -33.2) * mm, "end": v(103.05, -32.85) * mm});
            skLineSegment(sketch, "E386.1", {"start": v(103.05, -23.05) * mm, "end": v(103.05, -32.85) * mm});
            skLineSegment(sketch, "E386.2", {"start": v(102.55, -33.35) * mm, "end": v(92.75, -33.35) * mm});
            skLineSegment(sketch, "E386.3", {"start": v(92.75, -22.55) * mm, "end": v(102.55, -22.55) * mm});
            skArc(sketch, "E386.4", {"start": v(103.05, -23.05) * mm, "mid": v(102.9, -22.7) * mm, "end": v(102.55, -22.55) * mm});
            skArc(sketch, "E387.0", {"start": v(92.75, -22.55) * mm, "mid": v(92.4, -22.7) * mm, "end": v(92.25, -23.05) * mm});
            skArc(sketch, "E387.1", {"start": v(92.25, -32.85) * mm, "mid": v(92.4, -33.2) * mm, "end": v(92.75, -33.35) * mm});
            skLineSegment(sketch, "E387.2", {"start": v(96.65, -27.95) * mm, "end": v(98.65, -27.95) * mm});
            skLineSegment(sketch, "E387.3", {"start": v(97.65, -28.95) * mm, "end": v(97.65, -26.95) * mm});
            skLineSegment(sketch, "E387.4", {"start": v(92.25, -32.85) * mm, "end": v(92.25, -23.05) * mm});
            skLineSegment(sketch, "E388.0", {"start": v(76.05, -28.95) * mm, "end": v(76.05, -26.95) * mm});
            skLineSegment(sketch, "E388.1", {"start": v(70.65, -32.85) * mm, "end": v(70.65, -23.05) * mm});
            skLineSegment(sketch, "E388.2", {"start": v(81.45, -23.05) * mm, "end": v(81.45, -32.85) * mm});
            skLineSegment(sketch, "E388.3", {"start": v(71.15, -22.55) * mm, "end": v(80.95, -22.55) * mm});
            skLineSegment(sketch, "E388.4", {"start": v(80.95, -33.35) * mm, "end": v(71.15, -33.35) * mm});
            skLineSegment(sketch, "E388.5", {"start": v(75.05, -27.95) * mm, "end": v(77.05, -27.95) * mm});
            skArc(sketch, "E388.6", {"start": v(71.15, -22.55) * mm, "mid": v(70.8, -22.7) * mm, "end": v(70.65, -23.05) * mm});
            skArc(sketch, "E388.7", {"start": v(81.45, -23.05) * mm, "mid": v(81.3, -22.7) * mm, "end": v(80.95, -22.55) * mm});
            skArc(sketch, "E388.8", {"start": v(80.95, -33.35) * mm, "mid": v(81.3, -33.2) * mm, "end": v(81.45, -32.85) * mm});
            skArc(sketch, "E388.9", {"start": v(70.65, -32.85) * mm, "mid": v(70.8, -33.2) * mm, "end": v(71.15, -33.35) * mm});
            skLineSegment(sketch, "E389.0", {"start": v(-17.05, -27.95) * mm, "end": v(-15.05, -27.95) * mm});
            skLineSegment(sketch, "E389.1", {"start": v(-31.75, -22.55) * mm, "end": v(-0.35, -22.55) * mm});
            skLineSegment(sketch, "E389.2", {"start": v(-32.25, -32.85) * mm, "end": v(-32.25, -23.05) * mm});
            skLineSegment(sketch, "E389.3", {"start": v(-16.05, -28.95) * mm, "end": v(-16.05, -26.95) * mm});
            skLineSegment(sketch, "E389.4", {"start": v(-0.35, -33.35) * mm, "end": v(-31.75, -33.35) * mm});
            skLineSegment(sketch, "E389.5", {"start": v(0.15, -23.05) * mm, "end": v(0.15, -32.85) * mm});
            skArc(sketch, "E389.6", {"start": v(-31.75, -22.55) * mm, "mid": v(-32.1, -22.7) * mm, "end": v(-32.25, -23.05) * mm});
            skArc(sketch, "E389.7", {"start": v(-32.25, -32.85) * mm, "mid": v(-32.1, -33.2) * mm, "end": v(-31.75, -33.35) * mm});
            skArc(sketch, "E389.8", {"start": v(-0.35, -33.35) * mm, "mid": v(0, -33.2) * mm, "end": v(0.15, -32.85) * mm});
            skArc(sketch, "E389.9", {"start": v(0.15, -23.05) * mm, "mid": v(0, -22.7) * mm, "end": v(-0.35, -22.55) * mm});
            skLineSegment(sketch, "E390.0", {"start": v(-64.15, -22.55) * mm, "end": v(-43.55, -22.55) * mm});
            skLineSegment(sketch, "E390.1", {"start": v(-43.55, -33.35) * mm, "end": v(-64.15, -33.35) * mm});
            skLineSegment(sketch, "E390.2", {"start": v(-43.05, -23.05) * mm, "end": v(-43.05, -32.85) * mm});
            skLineSegment(sketch, "E390.3", {"start": v(-53.85, -28.95) * mm, "end": v(-53.85, -26.95) * mm});
            skLineSegment(sketch, "E390.4", {"start": v(-54.85, -27.95) * mm, "end": v(-52.85, -27.95) * mm});
            skLineSegment(sketch, "E390.5", {"start": v(-64.65, -32.85) * mm, "end": v(-64.65, -23.05) * mm});
            skArc(sketch, "E390.6", {"start": v(-64.65, -32.85) * mm, "mid": v(-64.5, -33.2) * mm, "end": v(-64.15, -33.35) * mm});
            skArc(sketch, "E390.7", {"start": v(-43.05, -23.05) * mm, "mid": v(-43.2, -22.7) * mm, "end": v(-43.55, -22.55) * mm});
            skArc(sketch, "E390.8", {"start": v(-43.55, -33.35) * mm, "mid": v(-43.2, -33.2) * mm, "end": v(-43.05, -32.85) * mm});
            skArc(sketch, "E390.9", {"start": v(-64.15, -22.55) * mm, "mid": v(-64.5, -22.7) * mm, "end": v(-64.65, -23.05) * mm});
            skLineSegment(sketch, "E391.0", {"start": v(-86.95, -27.95) * mm, "end": v(-84.95, -27.95) * mm});
            skLineSegment(sketch, "E391.1", {"start": v(-90.85, -22.55) * mm, "end": v(-81.05, -22.55) * mm});
            skLineSegment(sketch, "E391.2", {"start": v(-102.15, -23.05) * mm, "end": v(-102.15, -32.85) * mm});
            skLineSegment(sketch, "E391.3", {"start": v(-91.35, -32.85) * mm, "end": v(-91.35, -23.05) * mm});
            skLineSegment(sketch, "E391.4", {"start": v(-102.65, -33.35) * mm, "end": v(-112.45, -33.35) * mm});
            skLineSegment(sketch, "E391.5", {"start": v(-107.55, -28.95) * mm, "end": v(-107.55, -26.95) * mm});
            skLineSegment(sketch, "E391.6", {"start": v(-112.95, -32.85) * mm, "end": v(-112.95, -23.05) * mm});
            skLineSegment(sketch, "E391.7", {"start": v(-112.45, -22.55) * mm, "end": v(-102.65, -22.55) * mm});
            skLineSegment(sketch, "E391.8", {"start": v(-108.55, -27.95) * mm, "end": v(-106.55, -27.95) * mm});
            skLineSegment(sketch, "E391.9", {"start": v(-80.55, -23.05) * mm, "end": v(-80.55, -32.85) * mm});
            skLineSegment(sketch, "E391.10", {"start": v(-85.95, -28.95) * mm, "end": v(-85.95, -26.95) * mm});
            skLineSegment(sketch, "E391.11", {"start": v(-81.05, -33.35) * mm, "end": v(-90.85, -33.35) * mm});
            skArc(sketch, "E391.12", {"start": v(-91.35, -32.85) * mm, "mid": v(-91.2, -33.2) * mm, "end": v(-90.85, -33.35) * mm});
            skArc(sketch, "E391.13", {"start": v(-112.45, -22.55) * mm, "mid": v(-112.8, -22.7) * mm, "end": v(-112.95, -23.05) * mm});
            skArc(sketch, "E391.14", {"start": v(-90.85, -22.55) * mm, "mid": v(-91.2, -22.7) * mm, "end": v(-91.35, -23.05) * mm});
            skArc(sketch, "E391.15", {"start": v(-112.95, -32.85) * mm, "mid": v(-112.8, -33.2) * mm, "end": v(-112.45, -33.35) * mm});
            skArc(sketch, "E391.16", {"start": v(-102.65, -33.35) * mm, "mid": v(-102.3, -33.2) * mm, "end": v(-102.15, -32.85) * mm});
            skArc(sketch, "E391.17", {"start": v(-80.55, -23.05) * mm, "mid": v(-80.7, -22.7) * mm, "end": v(-81.05, -22.55) * mm});
            skArc(sketch, "E391.18", {"start": v(-81.05, -33.35) * mm, "mid": v(-80.7, -33.2) * mm, "end": v(-80.55, -32.85) * mm});
            skArc(sketch, "E391.19", {"start": v(-102.15, -23.05) * mm, "mid": v(-102.3, -22.7) * mm, "end": v(-102.65, -22.55) * mm});
            skLineSegment(sketch, "E392.0", {"start": v(-81.05, -55.55) * mm, "end": v(-90.85, -55.55) * mm});
            skLineSegment(sketch, "E392.1", {"start": v(-85.95, -51.15) * mm, "end": v(-85.95, -49.15) * mm});
            skLineSegment(sketch, "E392.2", {"start": v(-80.55, -45.25) * mm, "end": v(-80.55, -55.05) * mm});
            skLineSegment(sketch, "E392.3", {"start": v(-91.35, -55.05) * mm, "end": v(-91.35, -45.25) * mm});
            skLineSegment(sketch, "E392.4", {"start": v(-90.85, -44.75) * mm, "end": v(-81.05, -44.75) * mm});
            skLineSegment(sketch, "E392.5", {"start": v(-86.95, -50.15) * mm, "end": v(-84.95, -50.15) * mm});
            skArc(sketch, "E392.6", {"start": v(-81.05, -55.55) * mm, "mid": v(-80.7, -55.4) * mm, "end": v(-80.55, -55.05) * mm});
            skArc(sketch, "E392.7", {"start": v(-91.35, -55.05) * mm, "mid": v(-91.2, -55.4) * mm, "end": v(-90.85, -55.55) * mm});
            skArc(sketch, "E392.8", {"start": v(-90.85, -44.75) * mm, "mid": v(-91.2, -44.9) * mm, "end": v(-91.35, -45.25) * mm});
            skArc(sketch, "E392.9", {"start": v(-80.55, -45.25) * mm, "mid": v(-80.7, -44.9) * mm, "end": v(-81.05, -44.75) * mm});
            skLineSegment(sketch, "E393.0", {"start": v(-112.45, -44.75) * mm, "end": v(-102.65, -44.75) * mm});
            skLineSegment(sketch, "E393.1", {"start": v(-112.95, -55.05) * mm, "end": v(-112.95, -45.25) * mm});
            skLineSegment(sketch, "E393.2", {"start": v(-102.15, -45.25) * mm, "end": v(-102.15, -55.05) * mm});
            skLineSegment(sketch, "E393.3", {"start": v(-102.65, -55.55) * mm, "end": v(-112.45, -55.55) * mm});
            skLineSegment(sketch, "E393.4", {"start": v(-107.55, -51.15) * mm, "end": v(-107.55, -49.15) * mm});
            skLineSegment(sketch, "E393.5", {"start": v(-108.55, -50.15) * mm, "end": v(-106.55, -50.15) * mm});
            skArc(sketch, "E393.6", {"start": v(-112.95, -55.05) * mm, "mid": v(-112.8, -55.4) * mm, "end": v(-112.45, -55.55) * mm});
            skArc(sketch, "E393.7", {"start": v(-102.65, -55.55) * mm, "mid": v(-102.3, -55.4) * mm, "end": v(-102.15, -55.05) * mm});
            skArc(sketch, "E393.8", {"start": v(-102.15, -45.25) * mm, "mid": v(-102.3, -44.9) * mm, "end": v(-102.65, -44.75) * mm});
            skArc(sketch, "E393.9", {"start": v(-112.45, -44.75) * mm, "mid": v(-112.8, -44.9) * mm, "end": v(-112.95, -45.25) * mm});
            skLineSegment(sketch, "E394.0", {"start": v(-69.75, -55.05) * mm, "end": v(-69.75, -45.25) * mm});
            skLineSegment(sketch, "E394.1", {"start": v(16.65, -45.25) * mm, "end": v(16.65, -55.05) * mm});
            skLineSegment(sketch, "E394.2", {"start": v(-69.25, -44.75) * mm, "end": v(16.15, -44.75) * mm});
            skLineSegment(sketch, "E394.3", {"start": v(16.15, -55.55) * mm, "end": v(-69.25, -55.55) * mm});
            skLineSegment(sketch, "E394.4", {"start": v(-27.55, -50.15) * mm, "end": v(-25.55, -50.15) * mm});
            skLineSegment(sketch, "E394.5", {"start": v(-26.55, -51.15) * mm, "end": v(-26.55, -49.15) * mm});
            skArc(sketch, "E394.6", {"start": v(16.15, -55.55) * mm, "mid": v(16.5, -55.4) * mm, "end": v(16.65, -55.05) * mm});
            skArc(sketch, "E394.7", {"start": v(-69.25, -44.75) * mm, "mid": v(-69.6, -44.9) * mm, "end": v(-69.75, -45.25) * mm});
            skArc(sketch, "E394.8", {"start": v(-69.75, -55.05) * mm, "mid": v(-69.6, -55.4) * mm, "end": v(-69.25, -55.55) * mm});
            skArc(sketch, "E394.9", {"start": v(16.65, -45.25) * mm, "mid": v(16.5, -44.9) * mm, "end": v(16.15, -44.75) * mm});
            skCircle(sketch, "E395.0", {"center": v(134.67, 64) * mm, "radius": 1.75 * mm});
            skSolve(sketch);
        }
        {
            var Q0;
            Q0 = qSketchRegion(id + "F1", true);
            extrude(context, id + "F2", {"entities" : qUnion([Q0]), "depth" : 2 * mm, "offsetDistance" : 25 * mm});
        }
        {
            var Q0;
            Q0=makeQuery(id+"F2.opExtrude","CAP_FACE",FACE,{"disambiguationData":[OSD([sQuery(id+"F1.wireOp",EDGE,"E343.0"),sQuery(id+"F1.wireOp",EDGE,"E344.0"),sQuery(id+"F1.wireOp",EDGE,"E349.0"),sQuery(id+"F1.wireOp",EDGE,"E350.0"),sQuery(id+"F1.wireOp",EDGE,"E351.0"),sQuery(id+"F1.wireOp",EDGE,"E352.0"),sQuery(id+"F1.wireOp",EDGE,"E354.0"),sQuery(id+"F1.wireOp",EDGE,"E355.0"),sQuery(id+"F1.wireOp",EDGE,"E356.0"),sQuery(id+"F1.wireOp",EDGE,"E357.0"),sQuery(id+"F1.wireOp",EDGE,"E358.0"),sQuery(id+"F1.wireOp",EDGE,"E359.0"),sQuery(id+"F1.wireOp",EDGE,"E360.0"),sQuery(id+"F1.wireOp",EDGE,"E361.0"),sQuery(id+"F1.wireOp",EDGE,"E362.0"),sQuery(id+"F1.wireOp",EDGE,"E364.0"),sQuery(id+"F1.wireOp",EDGE,"E365.0"),sQuery(id+"F1.wireOp",EDGE,"E366.0"),sQuery(id+"F1.wireOp",EDGE,"E367.0"),sQuery(id+"F1.wireOp",EDGE,"E368.0"),sQuery(id+"F1.wireOp",EDGE,"E370.0"),sQuery(id+"F1.wireOp",EDGE,"E371.0"),sQuery(id+"F1.wireOp",EDGE,"E372.0"),sQuery(id+"F1.wireOp",EDGE,"E373.0"),sQuery(id+"F1.wireOp",EDGE,"E346.0"),sQuery(id+"F1.wireOp",EDGE,"E369.0.1"),sQuery(id+"F1.wireOp",EDGE,"E369.0.2"),sQuery(id+"F1.wireOp",EDGE,"E347.0"),sQuery(id+"F1.wireOp",EDGE,"E345.0"),sQuery(id+"F1.wireOp",EDGE,"E374.0"),sQuery(id+"F1.wireOp",EDGE,"E375.0"),sQuery(id+"F1.wireOp",EDGE,"E376.0"),sQuery(id+"F1.wireOp",EDGE,"E377.0"),sQuery(id+"F1.wireOp",EDGE,"E378.0"),sQuery(id+"F1.wireOp",EDGE,"E379.0"),sQuery(id+"F1.wireOp",EDGE,"E380.0"),sQuery(id+"F1.wireOp",EDGE,"E381.0"),sQuery(id+"F1.wireOp",EDGE,"E382.0"),sQuery(id+"F1.wireOp",EDGE,"E383.0"),sQuery(id+"F1.wireOp",EDGE,"E384.0"),sQuery(id+"F1.wireOp",EDGE,"E384.1"),sQuery(id+"F1.wireOp",EDGE,"E384.2"),sQuery(id+"F1.wireOp",EDGE,"E384.3"),sQuery(id+"F1.wireOp",EDGE,"E384.6"),sQuery(id+"F1.wireOp",EDGE,"E384.7"),sQuery(id+"F1.wireOp",EDGE,"E384.8"),sQuery(id+"F1.wireOp",EDGE,"E384.9"),sQuery(id+"F1.wireOp",EDGE,"E385.0"),sQuery(id+"F1.wireOp",EDGE,"E385.1"),sQuery(id+"F1.wireOp",EDGE,"E385.2"),sQuery(id+"F1.wireOp",EDGE,"E385.3"),sQuery(id+"F1.wireOp",EDGE,"E385.4"),sQuery(id+"F1.wireOp",EDGE,"E385.5"),sQuery(id+"F1.wireOp",EDGE,"E385.6"),sQuery(id+"F1.wireOp",EDGE,"E385.7"),sQuery(id+"F1.wireOp",EDGE,"E385.8"),sQuery(id+"F1.wireOp",EDGE,"E385.9"),sQuery(id+"F1.wireOp",EDGE,"E385.10"),sQuery(id+"F1.wireOp",EDGE,"E385.11"),sQuery(id+"F1.wireOp",EDGE,"E385.18"),sQuery(id+"F1.wireOp",EDGE,"E385.19"),sQuery(id+"F1.wireOp",EDGE,"E385.20"),sQuery(id+"F1.wireOp",EDGE,"E385.21"),sQuery(id+"F1.wireOp",EDGE,"E385.22"),sQuery(id+"F1.wireOp",EDGE,"E385.23"),sQuery(id+"F1.wireOp",EDGE,"E385.24"),sQuery(id+"F1.wireOp",EDGE,"E385.25"),sQuery(id+"F1.wireOp",EDGE,"E385.26"),sQuery(id+"F1.wireOp",EDGE,"E385.27"),sQuery(id+"F1.wireOp",EDGE,"E385.28"),sQuery(id+"F1.wireOp",EDGE,"E385.29"),sQuery(id+"F1.wireOp",EDGE,"E387.0"),sQuery(id+"F1.wireOp",EDGE,"E387.1"),sQuery(id+"F1.wireOp",EDGE,"E387.4"),sQuery(id+"F1.wireOp",EDGE,"E386.0"),sQuery(id+"F1.wireOp",EDGE,"E386.1"),sQuery(id+"F1.wireOp",EDGE,"E386.4"),sQuery(id+"F1.wireOp",EDGE,"E386.2"),sQuery(id+"F1.wireOp",EDGE,"E386.3"),sQuery(id+"F1.wireOp",EDGE,"E388.1"),sQuery(id+"F1.wireOp",EDGE,"E388.2"),sQuery(id+"F1.wireOp",EDGE,"E388.3"),sQuery(id+"F1.wireOp",EDGE,"E388.4"),sQuery(id+"F1.wireOp",EDGE,"E388.6"),sQuery(id+"F1.wireOp",EDGE,"E388.7"),sQuery(id+"F1.wireOp",EDGE,"E388.8"),sQuery(id+"F1.wireOp",EDGE,"E388.9"),sQuery(id+"F1.wireOp",EDGE,"E389.1"),sQuery(id+"F1.wireOp",EDGE,"E389.2"),sQuery(id+"F1.wireOp",EDGE,"E389.4"),sQuery(id+"F1.wireOp",EDGE,"E389.5"),sQuery(id+"F1.wireOp",EDGE,"E389.6"),sQuery(id+"F1.wireOp",EDGE,"E389.7"),sQuery(id+"F1.wireOp",EDGE,"E389.8"),sQuery(id+"F1.wireOp",EDGE,"E389.9"),sQuery(id+"F1.wireOp",EDGE,"E390.0"),sQuery(id+"F1.wireOp",EDGE,"E390.1"),sQuery(id+"F1.wireOp",EDGE,"E390.2"),sQuery(id+"F1.wireOp",EDGE,"E390.5"),sQuery(id+"F1.wireOp",EDGE,"E390.6"),sQuery(id+"F1.wireOp",EDGE,"E390.7"),sQuery(id+"F1.wireOp",EDGE,"E390.8"),sQuery(id+"F1.wireOp",EDGE,"E390.9"),sQuery(id+"F1.wireOp",EDGE,"E391.1"),sQuery(id+"F1.wireOp",EDGE,"E391.2"),sQuery(id+"F1.wireOp",EDGE,"E391.3"),sQuery(id+"F1.wireOp",EDGE,"E391.4"),sQuery(id+"F1.wireOp",EDGE,"E391.6"),sQuery(id+"F1.wireOp",EDGE,"E391.7"),sQuery(id+"F1.wireOp",EDGE,"E391.9"),sQuery(id+"F1.wireOp",EDGE,"E391.11"),sQuery(id+"F1.wireOp",EDGE,"E391.12"),sQuery(id+"F1.wireOp",EDGE,"E391.13"),sQuery(id+"F1.wireOp",EDGE,"E391.14"),sQuery(id+"F1.wireOp",EDGE,"E391.15"),sQuery(id+"F1.wireOp",EDGE,"E391.16"),sQuery(id+"F1.wireOp",EDGE,"E391.17"),sQuery(id+"F1.wireOp",EDGE,"E391.18"),sQuery(id+"F1.wireOp",EDGE,"E391.19"),sQuery(id+"F1.wireOp",EDGE,"E392.0"),sQuery(id+"F1.wireOp",EDGE,"E392.2"),sQuery(id+"F1.wireOp",EDGE,"E392.3"),sQuery(id+"F1.wireOp",EDGE,"E392.4"),sQuery(id+"F1.wireOp",EDGE,"E392.6"),sQuery(id+"F1.wireOp",EDGE,"E392.7"),sQuery(id+"F1.wireOp",EDGE,"E392.8"),sQuery(id+"F1.wireOp",EDGE,"E392.9"),sQuery(id+"F1.wireOp",EDGE,"E393.0"),sQuery(id+"F1.wireOp",EDGE,"E393.1"),sQuery(id+"F1.wireOp",EDGE,"E393.2"),sQuery(id+"F1.wireOp",EDGE,"E393.3"),sQuery(id+"F1.wireOp",EDGE,"E393.6"),sQuery(id+"F1.wireOp",EDGE,"E393.7"),sQuery(id+"F1.wireOp",EDGE,"E393.8"),sQuery(id+"F1.wireOp",EDGE,"E393.9"),sQuery(id+"F1.wireOp",EDGE,"E394.0"),sQuery(id+"F1.wireOp",EDGE,"E394.1"),sQuery(id+"F1.wireOp",EDGE,"E394.2"),sQuery(id+"F1.wireOp",EDGE,"E394.3"),sQuery(id+"F1.wireOp",EDGE,"E394.6"),sQuery(id+"F1.wireOp",EDGE,"E394.7"),sQuery(id+"F1.wireOp",EDGE,"E394.8"),sQuery(id+"F1.wireOp",EDGE,"E394.9"),sQuery(id+"F1.wireOp",EDGE,"E395.0")])],"isStart":true});
            var sketch = newSketch(context, id + "F3", { "sketchPlane" : qUnion([Q0])});
            skCircle(sketch, "E396.0", {"center": v(-96.65, 50.15) * mm, "radius": 3.5 * mm});
            skCircle(sketch, "E397.0", {"center": v(-96.65, 15.15) * mm, "radius": 3.5 * mm});
            skCircle(sketch, "E398.0", {"center": v(-38.65, 23.15) * mm, "radius": 3.5 * mm});
            skCircle(sketch, "E399.0", {"center": v(5.35, 17.15) * mm, "radius": 3.5 * mm});
            skCircle(sketch, "E400.0", {"center": v(-37, 2.54) * mm, "radius": 3.5 * mm});
            skCircle(sketch, "E401.0", {"center": v(21.35, 50.15) * mm, "radius": 3.5 * mm});
            skLineSegment(sketch, "E402.0.0", {"start": v(-139.2, -89.4) * mm, "end": v(-139.2, 88.4) * mm});
            skLineSegment(sketch, "E402.0.1", {"start": v(-139.2, 88.4) * mm, "end": v(-138.2, 88.4) * mm});
            skLineSegment(sketch, "E402.0.2", {"start": v(-138.2, 88.4) * mm, "end": v(140.2, 88.4) * mm});
            skLineSegment(sketch, "E402.0.3", {"start": v(140.2, 88.4) * mm, "end": v(140.2, -89.4) * mm});
            skLineSegment(sketch, "E402.0.4", {"start": v(140.2, -89.4) * mm, "end": v(-139.2, -89.4) * mm});
            skCircle(sketch, "E403.0", {"center": v(38, 2.54) * mm, "radius": 3.5 * mm});
            skCircle(sketch, "E404.0", {"center": v(38, -28.46) * mm, "radius": 3.5 * mm});
            skCircle(sketch, "E405.0", {"center": v(-37, -28.46) * mm, "radius": 3.5 * mm});
            skCircle(sketch, "E406.0", {"center": v(-45.05, -34.65) * mm, "radius": 3.5 * mm});
            skCircle(sketch, "E407.0", {"center": v(88.35, 23.15) * mm, "radius": 3.5 * mm});
            skCircle(sketch, "E408.0", {"center": v(110.35, 50.15) * mm, "radius": 3.5 * mm});
            skCircle(sketch, "E409.0", {"center": v(107.6, 3.75) * mm, "radius": 3.5 * mm});
            skCircle(sketch, "E410.0", {"center": v(110.85, -23.05) * mm, "radius": 3.5 * mm});
            skCircle(sketch, "E411.0", {"center": v(109.05, -33.65) * mm, "radius": 3.5 * mm});
            skCircle(sketch, "E412.0", {"center": v(45.8, -52.55) * mm, "radius": 3.5 * mm});
            skCircle(sketch, "E413.0", {"center": v(-2.2, -52.55) * mm, "radius": 3.5 * mm});
            skCircle(sketch, "E414.0", {"center": v(-50.2, -52.55) * mm, "radius": 3.5 * mm});
            skCircle(sketch, "E415.0", {"center": v(-89.45, -33.55) * mm, "radius": 3.5 * mm});
            skCircle(sketch, "E416.0", {"center": v(-89.45, -6.55) * mm, "radius": 3.5 * mm});
            skSolve(sketch);
        }
        {
            var Q0;
            Q0=makeQuery(id+"F3.imprint","IMPRINT",FACE,{"disambiguationData":[TD([[makeQuery(id+"F3.imprint","IMPRINT",EDGE,{"derivedFrom":sQuery(id+"F3.wireOp",EDGE,"E396.0")}),-1.0]])]});
            var sketch = newSketch(context, id + "F4", { "sketchPlane" : qUnion([Q0])});
            skPoint(sketch, "E417.0", {"position": v(109.05, -33.65) * mm});
            skPoint(sketch, "E418.0", {"position": v(110.85, -23.05) * mm});
            skPoint(sketch, "E419.0", {"position": v(107.6, 3.75) * mm});
            skPoint(sketch, "E420.0", {"position": v(38, -28.46) * mm});
            skPoint(sketch, "E421.0", {"position": v(45.8, -52.55) * mm});
            skPoint(sketch, "E422.0", {"position": v(-2.2, -52.55) * mm});
            skPoint(sketch, "E423.0", {"position": v(-50.2, -52.55) * mm});
            skPoint(sketch, "E424.0", {"position": v(-45.05, -34.65) * mm});
            skPoint(sketch, "E425.0", {"position": v(-37, -28.46) * mm});
            skPoint(sketch, "E426.0", {"position": v(-89.45, -33.55) * mm});
            skPoint(sketch, "E427.0", {"position": v(-37, 2.54) * mm});
            skPoint(sketch, "E428.0", {"position": v(38, 2.54) * mm});
            skPoint(sketch, "E429.0", {"position": v(88.35, 23.15) * mm});
            skPoint(sketch, "E430.0", {"position": v(110.35, 50.15) * mm});
            skPoint(sketch, "E431.0", {"position": v(21.35, 50.15) * mm});
            skPoint(sketch, "E432.0", {"position": v(5.35, 17.15) * mm});
            skPoint(sketch, "E433.0", {"position": v(-38.65, 23.15) * mm});
            skPoint(sketch, "E434.0", {"position": v(-96.65, 15.15) * mm});
            skPoint(sketch, "E435.0", {"position": v(-89.45, -6.55) * mm});
            skPoint(sketch, "E436.0", {"position": v(-96.65, 50.15) * mm});
            skCircle(sketch, "E437", {"center": v(45.8, -52.55) * mm, "radius": 2.5 * mm});
            skCircle(sketch, "E438", {"center": v(-2.2, -52.55) * mm, "radius": 2.5 * mm});
            skCircle(sketch, "E439", {"center": v(-50.2, -52.55) * mm, "radius": 2.5 * mm});
            skCircle(sketch, "E440", {"center": v(-45.05, -34.65) * mm, "radius": 2.5 * mm});
            skCircle(sketch, "E441", {"center": v(-37, -28.46) * mm, "radius": 2.5 * mm});
            skCircle(sketch, "E442", {"center": v(38, -28.46) * mm, "radius": 2.5 * mm});
            skCircle(sketch, "E443", {"center": v(-37, 2.54) * mm, "radius": 2.5 * mm});
            skCircle(sketch, "E444", {"center": v(38, 2.54) * mm, "radius": 2.5 * mm});
            skCircle(sketch, "E445", {"center": v(-89.45, -33.55) * mm, "radius": 2.5 * mm});
            skCircle(sketch, "E446", {"center": v(-89.45, -6.55) * mm, "radius": 2.5 * mm});
            skCircle(sketch, "E447", {"center": v(-96.65, 15.15) * mm, "radius": 2.5 * mm});
            skCircle(sketch, "E448", {"center": v(-38.65, 23.15) * mm, "radius": 2.5 * mm});
            skCircle(sketch, "E449", {"center": v(5.35, 17.15) * mm, "radius": 2.5 * mm});
            skCircle(sketch, "E450", {"center": v(21.35, 50.15) * mm, "radius": 2.5 * mm});
            skCircle(sketch, "E451", {"center": v(88.35, 23.15) * mm, "radius": 2.5 * mm});
            skCircle(sketch, "E452", {"center": v(107.6, 3.75) * mm, "radius": 2.5 * mm});
            skCircle(sketch, "E453", {"center": v(110.85, -23.05) * mm, "radius": 2.5 * mm});
            skCircle(sketch, "E454", {"center": v(109.05, -33.65) * mm, "radius": 2.5 * mm});
            skCircle(sketch, "E455", {"center": v(110.35, 50.15) * mm, "radius": 2.5 * mm});
            skCircle(sketch, "E456", {"center": v(-96.65, 50.15) * mm, "radius": 2.5 * mm});
            skSolve(sketch);
        }
        {
            var Q0;
            Q0=makeQuery(id+"F4.imprint","IMPRINT",FACE,{"disambiguationData":[TD([[makeQuery(id+"F4.imprint","IMPRINT",EDGE,{"derivedFrom":sQuery(id+"F4.wireOp",EDGE,"E441")}),1.0]])]});
            var Q1;
            Q1=makeQuery(id+"F4.imprint","IMPRINT",FACE,{"disambiguationData":[TD([[makeQuery(id+"F4.imprint","IMPRINT",EDGE,{"derivedFrom":sQuery(id+"F4.wireOp",EDGE,"E443")}),1.0]])]});
            var Q2;
            Q2=makeQuery(id+"F4.imprint","IMPRINT",FACE,{"disambiguationData":[TD([[makeQuery(id+"F4.imprint","IMPRINT",EDGE,{"derivedFrom":sQuery(id+"F4.wireOp",EDGE,"E444")}),1.0]])]});
            var Q3;
            Q3=makeQuery(id+"F4.imprint","IMPRINT",FACE,{"disambiguationData":[TD([[makeQuery(id+"F4.imprint","IMPRINT",EDGE,{"derivedFrom":sQuery(id+"F4.wireOp",EDGE,"E442")}),1.0]])]});
            extrude(context, id + "F5", {"entities" : qUnion([Q0, Q1, Q2, Q3]), "operationType" : NewBodyOperationType.ADD, "depth" : 6 * mm, "offsetDistance" : 25 * mm});
        }
        {
            var Q0;
            Q0=makeQuery(id+"F4.imprint","IMPRINT",FACE,{"disambiguationData":[TD([[makeQuery(id+"F4.imprint","IMPRINT",EDGE,{"derivedFrom":sQuery(id+"F4.wireOp",EDGE,"E437")}),1.0]])]});
            var Q1;
            Q1=makeQuery(id+"F4.imprint","IMPRINT",FACE,{"disambiguationData":[TD([[makeQuery(id+"F4.imprint","IMPRINT",EDGE,{"derivedFrom":sQuery(id+"F4.wireOp",EDGE,"E454")}),1.0]])]});
            var Q2;
            Q2=makeQuery(id+"F4.imprint","IMPRINT",FACE,{"disambiguationData":[TD([[makeQuery(id+"F4.imprint","IMPRINT",EDGE,{"derivedFrom":sQuery(id+"F4.wireOp",EDGE,"E453")}),1.0]])]});
            var Q3;
            Q3=makeQuery(id+"F4.imprint","IMPRINT",FACE,{"disambiguationData":[TD([[makeQuery(id+"F4.imprint","IMPRINT",EDGE,{"derivedFrom":sQuery(id+"F4.wireOp",EDGE,"E452")}),1.0]])]});
            var Q4;
            Q4=makeQuery(id+"F4.imprint","IMPRINT",FACE,{"disambiguationData":[TD([[makeQuery(id+"F4.imprint","IMPRINT",EDGE,{"derivedFrom":sQuery(id+"F4.wireOp",EDGE,"E451")}),1.0]])]});
            var Q5;
            Q5=makeQuery(id+"F4.imprint","IMPRINT",FACE,{"disambiguationData":[TD([[makeQuery(id+"F4.imprint","IMPRINT",EDGE,{"derivedFrom":sQuery(id+"F4.wireOp",EDGE,"E455")}),1.0]])]});
            var Q6;
            Q6=makeQuery(id+"F4.imprint","IMPRINT",FACE,{"disambiguationData":[TD([[makeQuery(id+"F4.imprint","IMPRINT",EDGE,{"derivedFrom":sQuery(id+"F4.wireOp",EDGE,"E450")}),1.0]])]});
            var Q7;
            Q7=makeQuery(id+"F4.imprint","IMPRINT",FACE,{"disambiguationData":[TD([[makeQuery(id+"F4.imprint","IMPRINT",EDGE,{"derivedFrom":sQuery(id+"F4.wireOp",EDGE,"E449")}),1.0]])]});
            var Q8;
            Q8=makeQuery(id+"F4.imprint","IMPRINT",FACE,{"disambiguationData":[TD([[makeQuery(id+"F4.imprint","IMPRINT",EDGE,{"derivedFrom":sQuery(id+"F4.wireOp",EDGE,"E448")}),1.0]])]});
            var Q9;
            Q9=makeQuery(id+"F4.imprint","IMPRINT",FACE,{"disambiguationData":[TD([[makeQuery(id+"F4.imprint","IMPRINT",EDGE,{"derivedFrom":sQuery(id+"F4.wireOp",EDGE,"E447")}),1.0]])]});
            var Q10;
            Q10=makeQuery(id+"F4.imprint","IMPRINT",FACE,{"disambiguationData":[TD([[makeQuery(id+"F4.imprint","IMPRINT",EDGE,{"derivedFrom":sQuery(id+"F4.wireOp",EDGE,"E456")}),1.0]])]});
            var Q11;
            Q11=makeQuery(id+"F4.imprint","IMPRINT",FACE,{"disambiguationData":[TD([[makeQuery(id+"F4.imprint","IMPRINT",EDGE,{"derivedFrom":sQuery(id+"F4.wireOp",EDGE,"E446")}),1.0]])]});
            var Q12;
            Q12=makeQuery(id+"F4.imprint","IMPRINT",FACE,{"disambiguationData":[TD([[makeQuery(id+"F4.imprint","IMPRINT",EDGE,{"derivedFrom":sQuery(id+"F4.wireOp",EDGE,"E445")}),1.0]])]});
            var Q13;
            Q13=makeQuery(id+"F4.imprint","IMPRINT",FACE,{"disambiguationData":[TD([[makeQuery(id+"F4.imprint","IMPRINT",EDGE,{"derivedFrom":sQuery(id+"F4.wireOp",EDGE,"E440")}),1.0]])]});
            var Q14;
            Q14=makeQuery(id+"F4.imprint","IMPRINT",FACE,{"disambiguationData":[TD([[makeQuery(id+"F4.imprint","IMPRINT",EDGE,{"derivedFrom":sQuery(id+"F4.wireOp",EDGE,"E439")}),1.0]])]});
            var Q15;
            Q15=makeQuery(id+"F4.imprint","IMPRINT",FACE,{"disambiguationData":[TD([[makeQuery(id+"F4.imprint","IMPRINT",EDGE,{"derivedFrom":sQuery(id+"F4.wireOp",EDGE,"E438")}),1.0]])]});
            extrude(context, id + "F6", {"entities" : qUnion([Q0, Q1, Q2, Q3, Q4, Q5, Q6, Q7, Q8, Q9, Q10, Q11, Q12, Q13, Q14, Q15]), "operationType" : NewBodyOperationType.ADD, "depth" : 5 * mm, "offsetDistance" : 25 * mm});
        }
    });
